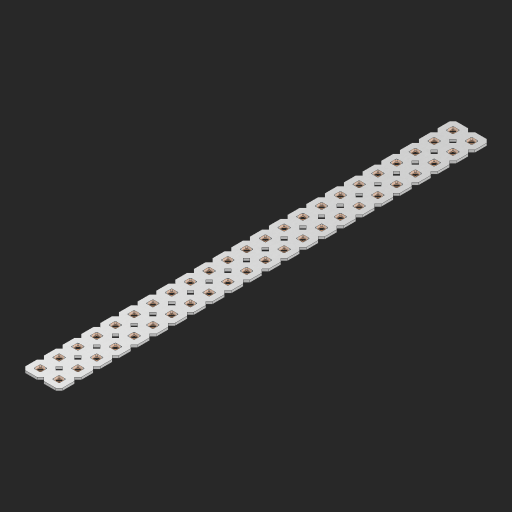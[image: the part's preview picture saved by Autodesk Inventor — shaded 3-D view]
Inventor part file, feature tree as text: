
AUTODESK INVENTOR PART (.ipt)
format: ipt  version: 2023 (Build 270158000, 158)  size: 802,816 bytes
history: native  units: in
note: dims shown in document units (in); Inventor stores cm internally (conversion verified against a paired STEP export)
features: other x47, extrude x45, sketch x2, pattern_linear x1
ambient origin geometry x8: Origin, YZ Plane, XZ Plane, XY Plane, X Axis, Y Axis, Z Axis, Center Point
bodies: Solid1 (feature_tree), Body (feature_tree)
feature tree (95):
  pattern_linear  "Rectangular Pattern1"  Spacing1=0.09in  [1 undecoded]
  sketch  "Sketch1"  dims[d1=0.5in]
  sketch  "Sketch2"  dims[d2=0.182in d3=0.09in d4=0.09in d5=0.09in d6=0.09in d7=0.09in d8=0.09in d9=0.09in d10=0.09in d11=0.02in d13=0.0in d14=0.172in d15=0.0625in d16=0.0in d19=0.5in d22=0.5in]
  other  "Srf1"
  other  "Srf126"
  other  "Srf127"
  other  "Srf128"
  other  "Srf129"
  other  "Srf130"
  other  "Srf131"
  other  "Srf250"
  other  "Srf251"
  other  "Srf252"
  other  "Srf253"
  other  "Srf254"
  other  "Srf255"
  other  "Srf256"
  other  "Srf257"
  other  "Srf258"
  other  "Srf259"
  other  "Srf260"
  other  "Srf261"
  other  "Srf262"
  other  "Srf263"
  other  "Srf264"
  other  "Srf265"
  other  "Srf268"
  other  "Srf269"
  other  "Srf270"
  other  "Srf271"
  other  "Srf272"
  other  "Srf273"
  other  "Srf274"
  other  "Srf275"
  other  "Srf276"
  other  "Srf277"
  other  "Srf278"
  other  "Srf279"
  other  "Srf280"
  other  "Srf281"
  other  "Srf282"
  other  "Srf283"
  other  "Srf284"
  other  "Srf285"
  other  "Srf286"
  other  "Srf287"
  other  "Srf288"
  other  "Srf289"
  other  "Srf290"
  other  "Circle"
  extrude  "ExtrusionSrf126"  Depth=0.09in
  extrude  "ExtrusionSrf127"  Depth=0.09in
  extrude  "ExtrusionSrf128"  Depth=0.09in
  extrude  "ExtrusionSrf129"  Depth=0.09in
  extrude  "ExtrusionSrf130"  Depth=0.09in
  extrude  "ExtrusionSrf131"  Depth=0.09in
  extrude  "ExtrusionSrf250"  Depth=0.09in
  extrude  "ExtrusionSrf251"  Depth=0.02in
  extrude  "ExtrusionSrf252"  TaperAngle=0.0deg  [1 undecoded]
  extrude  "ExtrusionSrf253"  Depth=0.5in
  extrude  "ExtrusionSrf254"  Depth=0.0625in TaperAngle=0.0deg
  extrude  "ExtrusionSrf255"  Depth=0.5in
  extrude  "ExtrusionSrf256"  Depth=0.5in
  extrude  "ExtrusionSrf257"  [1 undecoded]
  extrude  "ExtrusionSrf258"  [1 undecoded]
  extrude  "ExtrusionSrf259"  [1 undecoded]
  extrude  "ExtrusionSrf260"  [1 undecoded]
  extrude  "ExtrusionSrf261"  [1 undecoded]
  extrude  "ExtrusionSrf262"  [1 undecoded]
  extrude  "ExtrusionSrf263"  [1 undecoded]
  extrude  "ExtrusionSrf264"  [1 undecoded]
  extrude  "ExtrusionSrf265"  [1 undecoded]
  extrude  "ExtrusionSrf268"  [1 undecoded]
  extrude  "ExtrusionSrf269"  [1 undecoded]
  extrude  "ExtrusionSrf270"  [1 undecoded]
  extrude  "ExtrusionSrf271"  [1 undecoded]
  extrude  "ExtrusionSrf272"  [1 undecoded]
  extrude  "ExtrusionSrf273"  [1 undecoded]
  extrude  "ExtrusionSrf274"  [1 undecoded]
  extrude  "ExtrusionSrf275"  [1 undecoded]
  extrude  "ExtrusionSrf276"  [1 undecoded]
  extrude  "ExtrusionSrf277"  [1 undecoded]
  extrude  "ExtrusionSrf278"  [1 undecoded]
  extrude  "ExtrusionSrf279"  [1 undecoded]
  extrude  "ExtrusionSrf280"  [1 undecoded]
  extrude  "ExtrusionSrf281"  [1 undecoded]
  extrude  "ExtrusionSrf282"  [1 undecoded]
  extrude  "ExtrusionSrf283"  [1 undecoded]
  extrude  "ExtrusionSrf284"  [1 undecoded]
  extrude  "ExtrusionSrf285"  [1 undecoded]
  extrude  "ExtrusionSrf286"  [1 undecoded]
  extrude  "ExtrusionSrf287"  [1 undecoded]
  extrude  "ExtrusionSrf288"  [1 undecoded]
  extrude  "ExtrusionSrf289"  [1 undecoded]
  extrude  "ExtrusionSrf290"  [1 undecoded]
note: 34 required parameter values undecoded (feature->parameter linkage not recoverable at this tier; creation-order binding heuristic only, values carry confidence <= 0.55)
